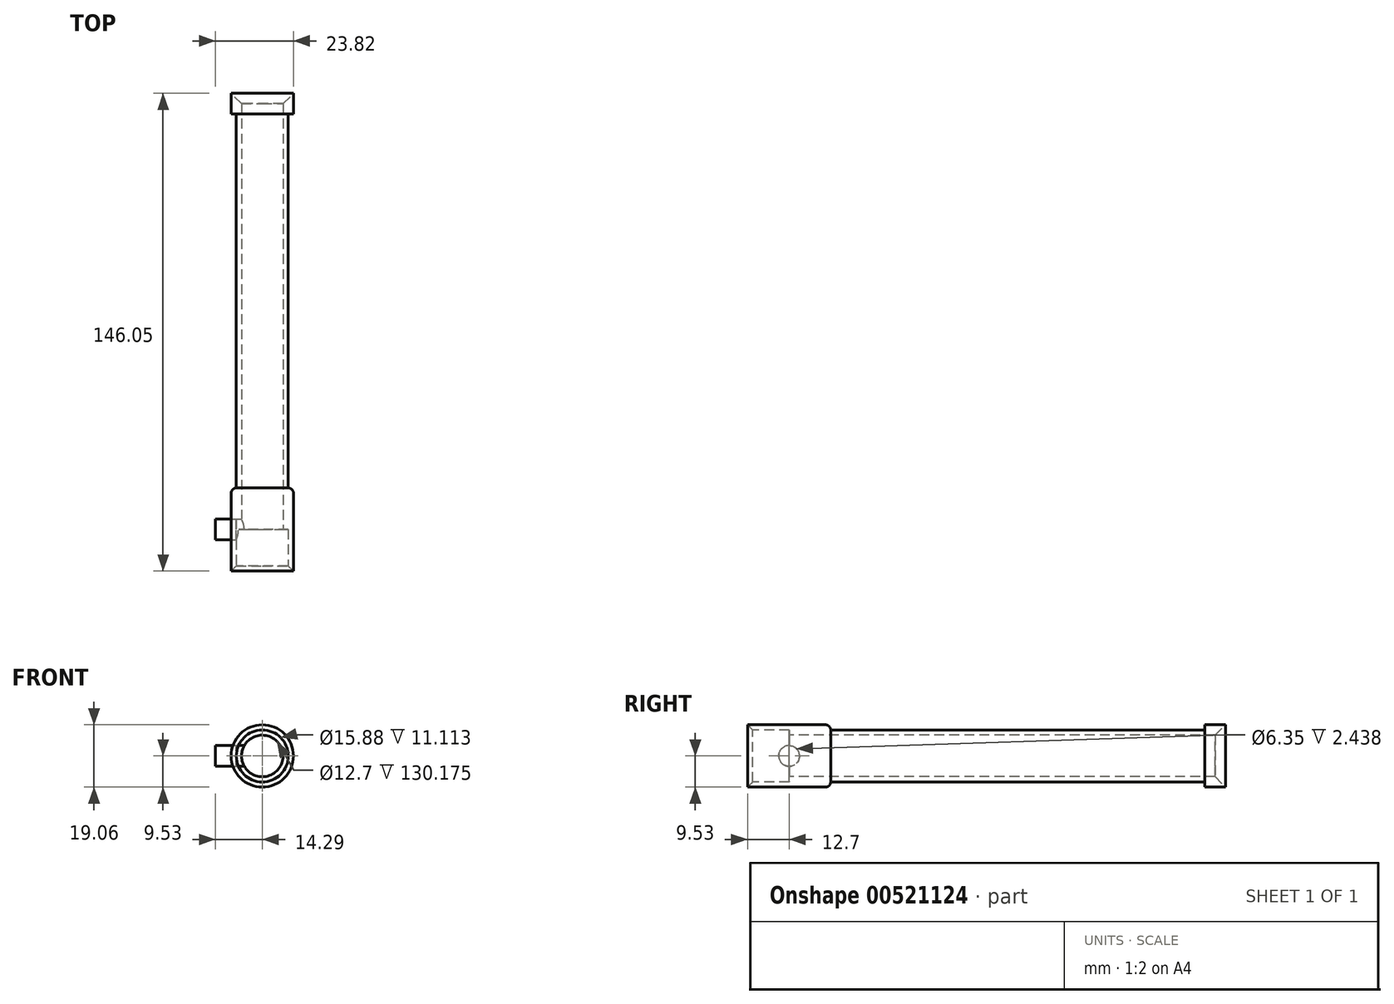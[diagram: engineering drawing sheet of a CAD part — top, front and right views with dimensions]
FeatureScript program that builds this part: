
annotation { "Feature Type Name" : "Feature", "Feature Type Description" : "" }
export const myFeature = defineFeature(function(context is Context, id is Id, definition is map)
    precondition{}
    {
        {
            var Q0;
            Q0=qCreatedBy(makeId("Right.planeOp"),FACE);
            var sketch = newSketch(context, id + "F0", { "sketchPlane" : qUnion([Q0])});
            skLineSegment(sketch, "E0.bottom", {"start": v(0, 7.94) * mm, "end": v(12.7, 7.94) * mm});
            skLineSegment(sketch, "E0.top", {"start": v(0, 9.53) * mm, "end": v(25.4, 9.53) * mm});
            skLineSegment(sketch, "E0.left", {"start": v(0, 7.94) * mm, "end": v(0, 9.53) * mm});
            skLineSegment(sketch, "E0.right", {"start": v(25.4, 7.94) * mm, "end": v(25.4, 9.53) * mm});
            skLineSegment(sketch, "E1.bottom", {"start": v(25.4, 7.94) * mm, "end": v(139.7, 7.94) * mm});
            skLineSegment(sketch, "E1.top", {"start": v(12.7, 6.35) * mm, "end": v(146.05, 6.35) * mm});
            skLineSegment(sketch, "E1.left", {"start": v(12.7, 7.94) * mm, "end": v(12.7, 6.35) * mm});
            skLineSegment(sketch, "E1.right", {"start": v(146.05, 7.94) * mm, "end": v(146.05, 6.35) * mm});
            skLineSegment(sketch, "E2.bottom", {"start": v(146.05, 9.53) * mm, "end": v(139.7, 9.53) * mm});
            skLineSegment(sketch, "E2.left", {"start": v(146.05, 9.53) * mm, "end": v(146.05, 7.94) * mm});
            skLineSegment(sketch, "E2.right", {"start": v(139.7, 9.53) * mm, "end": v(139.7, 7.94) * mm});
            skLineSegment(sketch, "E3", {"start": v(0, 0) * mm, "end": v(42.33, 0) * mm, "construction": true});
            skSolve(sketch);
        }
        {
            var Q0;
            Q0=makeQuery(id+"F0.imprint","IMPRINT",FACE,{"disambiguationData":[TD([[makeQuery(id+"F0.imprint","IMPRINT",EDGE,{"derivedFrom":sQuery(id+"F0.wireOp",EDGE,"E0.bottom")}),1.0]])]});
            var Q1;
            Q1=sQuery(id+"F0.wireOp",EDGE,"E3");
            revolve(context, id + "F1", {"entities" : qUnion([Q0]), "axis" : qUnion([Q1]), "revolveType" : RevolveType.FULL});
        }
        {
            var Q0;
            Q0=makeQuery(id+"F1.opRevolve","SWEPT_EDGE",EDGE,{"disambiguationData":[OSD([sQuery(id+"F0.wireOp",EDGE,"E0.bottom"),sQuery(id+"F0.wireOp",EDGE,"E0.left")])]});
            chamfer(context, id + "F2", {"entities" : qUnion([Q0]), "width" : 1.59 * mm, "tangentPropagation" : true});
        }
        {
            var Q0;
            Q0=makeQuery(id+"F1.opRevolve","SWEPT_EDGE",EDGE,{"disambiguationData":[OSD([sQuery(id+"F0.wireOp",EDGE,"E1.top"),sQuery(id+"F0.wireOp",EDGE,"E1.right")])]});
            chamfer(context, id + "F3", {"entities" : qUnion([Q0]), "width" : 3.17 * mm, "tangentPropagation" : true});
        }
        {
            var Q0;
            Q0=makeQuery(id+"F1.opRevolve","SWEPT_EDGE",EDGE,{"disambiguationData":[OSD([sQuery(id+"F0.wireOp",EDGE,"E0.top"),sQuery(id+"F0.wireOp",EDGE,"E0.right")])]});
            fillet(context, id + "F4", {"entities" : qUnion([Q0]), "radius" : 1.59 * mm, "tangentPropagation" : true, "allowEdgeOverflow" : false});
        }
        {
            var Q0;
            Q0=qCreatedBy(makeId("Right.planeOp"),FACE);
            var sketch = newSketch(context, id + "F5", { "sketchPlane" : qUnion([Q0])});
            skCircle(sketch, "E4", {"center": v(12.7, 0) * mm, "radius": 3.18 * mm});
            skSolve(sketch);
        }
        {
            var Q0;
            Q0=makeQuery(id+"F5.imprint","IMPRINT",FACE,{"disambiguationData":[TD([[makeQuery(id+"F5.imprint","IMPRINT",EDGE,{"derivedFrom":sQuery(id+"F5.wireOp",EDGE,"E4")}),1.0]])]});
            extrude(context, id + "F6", {"entities" : qUnion([Q0]), "oppositeDirection" : true, "depth" : 14.29 * mm, "offsetDistance" : 25.4 * mm});
        }
        {
            var Q0;
            Q0 = qSketchRegion(id + "F5", true);
            extrude(context, id + "F7", {"entities" : qUnion([Q0]), "operationType" : NewBodyOperationType.REMOVE, "oppositeDirection" : true, "depth" : 7.94 * mm, "offsetDistance" : 25.4 * mm});
        }
    });
